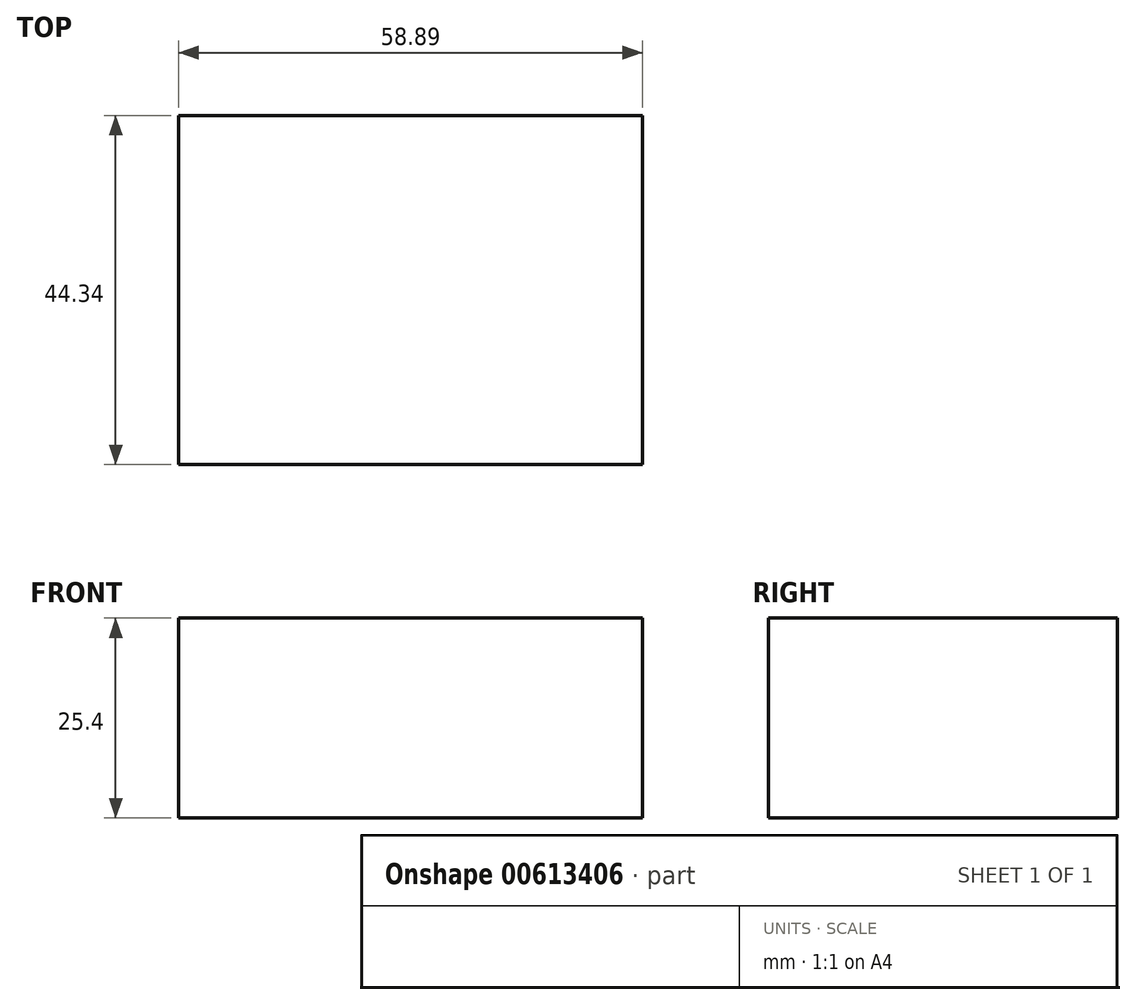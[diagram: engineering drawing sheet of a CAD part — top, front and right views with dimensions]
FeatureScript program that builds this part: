
annotation { "Feature Type Name" : "Feature", "Feature Type Description" : "" }
export const myFeature = defineFeature(function(context is Context, id is Id, definition is map)
    precondition{}
    {
        {
            var Q0;
            Q0=qCreatedBy(makeId("Top.planeOp"),FACE);
            var sketch = newSketch(context, id + "F0", { "sketchPlane" : qUnion([Q0])});
            skLineSegment(sketch, "E0.bottom", {"start": v(-40.54, -10.04) * mm, "end": v(18.35, -10.04) * mm});
            skLineSegment(sketch, "E0.top", {"start": v(-40.54, 34.3) * mm, "end": v(18.35, 34.3) * mm});
            skLineSegment(sketch, "E0.left", {"start": v(-40.54, -10.04) * mm, "end": v(-40.54, 34.3) * mm});
            skLineSegment(sketch, "E0.right", {"start": v(18.35, -10.04) * mm, "end": v(18.35, 34.3) * mm});
            skSolve(sketch);
        }
        {
            var Q0;
            Q0=makeQuery(id+"F0.imprint","IMPRINT",FACE,{"disambiguationData":[TD([[makeQuery(id+"F0.imprint","IMPRINT",EDGE,{"derivedFrom":sQuery(id+"F0.wireOp",EDGE,"E0.bottom")}),1.0]])]});
            extrude(context, id + "F1", {"entities" : qUnion([Q0]), "depth" : 25.4 * mm, "offsetDistance" : 25.4 * mm});
        }
    });
